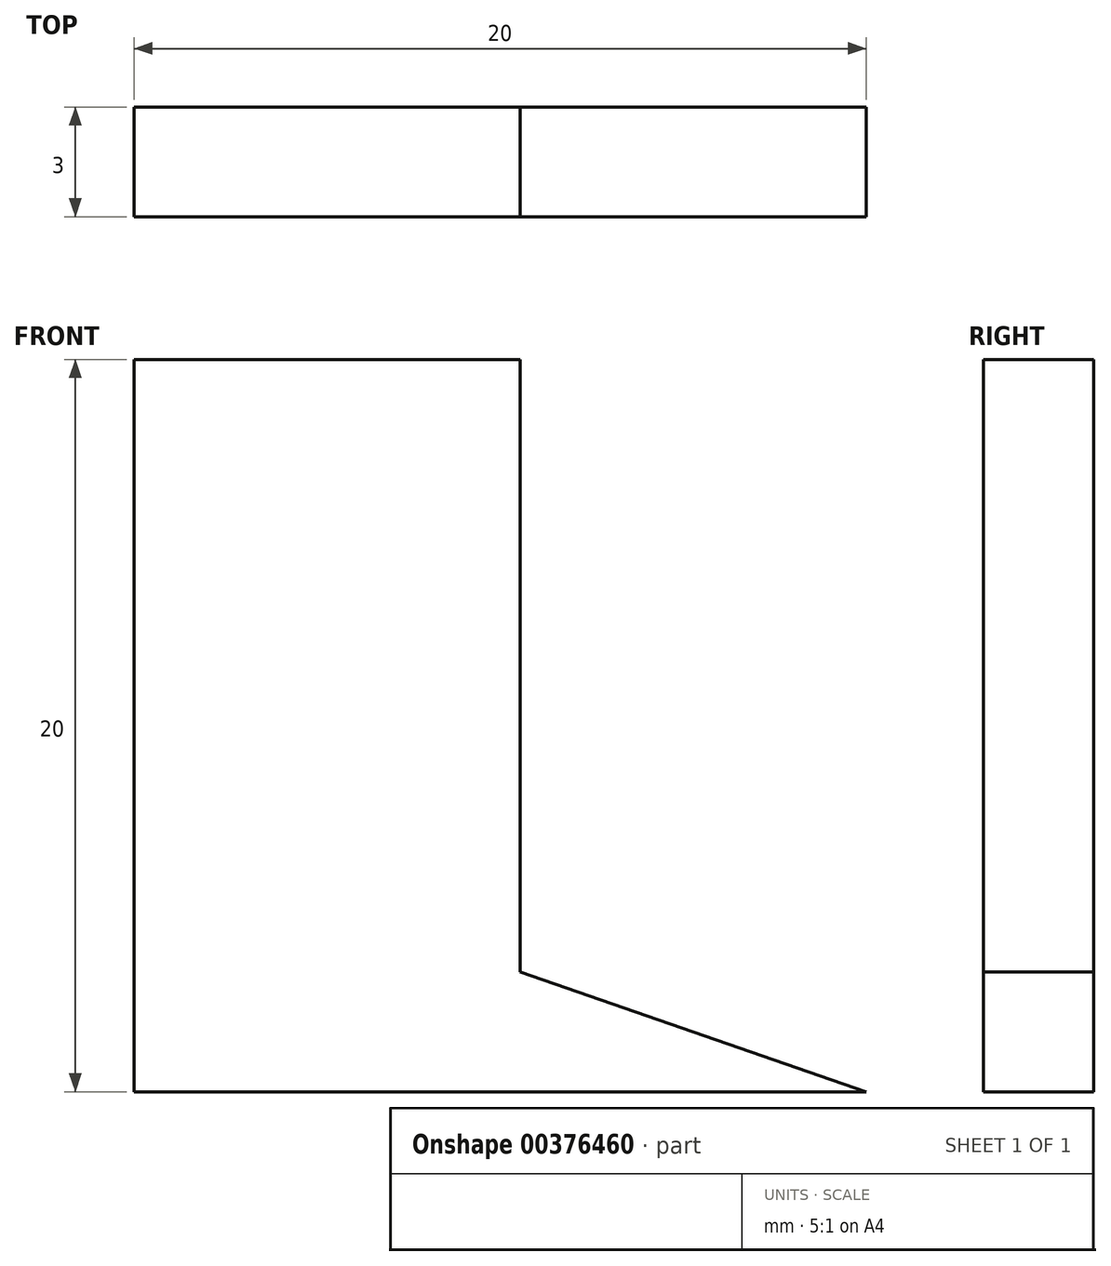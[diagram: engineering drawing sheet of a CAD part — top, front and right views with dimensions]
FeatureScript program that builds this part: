
annotation { "Feature Type Name" : "Feature", "Feature Type Description" : "" }
export const myFeature = defineFeature(function(context is Context, id is Id, definition is map)
    precondition{}
    {
        {
            var Q0;
            Q0=qCreatedBy(makeId("Front.planeOp"),FACE);
            var sketch = newSketch(context, id + "F0", { "sketchPlane" : qUnion([Q0])});
            skLineSegment(sketch, "E0", {"start": v(0, 0) * mm, "end": v(0, 20) * mm});
            skLineSegment(sketch, "E1", {"start": v(0, 0) * mm, "end": v(20, 0) * mm});
            skLineSegment(sketch, "E2", {"start": v(20, 0) * mm, "end": v(10.55, 3.27) * mm});
            skLineSegment(sketch, "E3", {"start": v(10.55, 3.27) * mm, "end": v(10.55, 20) * mm});
            skLineSegment(sketch, "E4", {"start": v(0, 20) * mm, "end": v(10.55, 20) * mm});
            skSolve(sketch);
        }
        {
            var Q0;
            Q0 = qSketchRegion(id + "F0", true);
            extrude(context, id + "F1", {"entities" : qUnion([Q0]), "depth" : 3 * mm});
        }
    });
